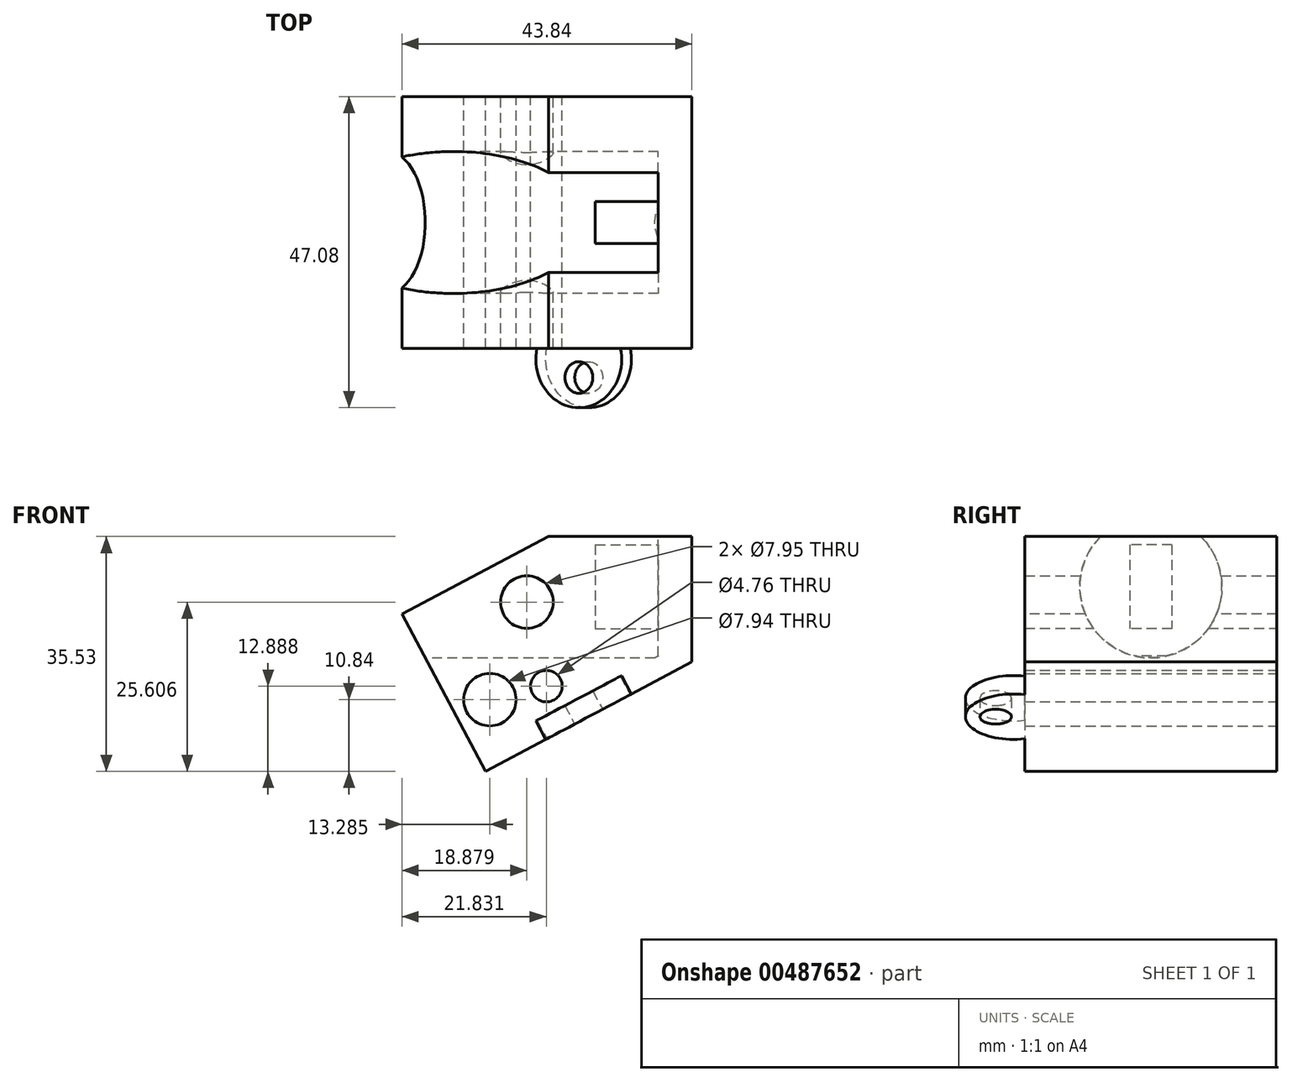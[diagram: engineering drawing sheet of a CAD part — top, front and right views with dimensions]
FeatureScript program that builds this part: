
annotation { "Feature Type Name" : "Feature", "Feature Type Description" : "" }
export const myFeature = defineFeature(function(context is Context, id is Id, definition is map)
    precondition{}
    {
        {
            var Q0;
            Q0=qCreatedBy(makeId("Top.planeOp"),FACE);
            var sketch = newSketch(context, id + "F0", { "sketchPlane" : qUnion([Q0])});
            skLineSegment(sketch, "E0.bottom", {"start": v(0, 0) * mm, "end": v(50.8, 0) * mm});
            skLineSegment(sketch, "E0.top", {"start": v(0, -38.1) * mm, "end": v(50.8, -38.1) * mm});
            skLineSegment(sketch, "E0.left", {"start": v(0, 0) * mm, "end": v(0, -38.1) * mm});
            skLineSegment(sketch, "E0.right", {"start": v(50.8, 0) * mm, "end": v(50.8, -38.1) * mm});
            skSolve(sketch);
        }
        {
            var Q0;
            Q0 = qSketchRegion(id + "F0", true);
            extrude(context, id + "F1", {"entities" : qUnion([Q0]), "depth" : 50.8 * mm, "offsetDistance" : 25.4 * mm});
        }
        {
            var Q0;
            Q0=makeQuery(id+"F1.opExtrude","SWEPT_FACE",FACE,{"disambiguationData":[OSD([sQuery(id+"F0.wireOp",EDGE,"E0.top")])]});
            var sketch = newSketch(context, id + "F2", { "sketchPlane" : qUnion([Q0])});
            skLineSegment(sketch, "E1", {"start": v(29.5, 53.9) * mm, "end": v(29.5, 32.46) * mm, "construction": true});
            skLineSegment(sketch, "E2", {"start": v(45.7, 53.9) * mm, "end": v(45.7, 32.46) * mm});
            skLineSegment(sketch, "E3", {"start": v(29.5, 32.46) * mm, "end": v(5.38, 32.46) * mm, "construction": true});
            skLineSegment(sketch, "E4", {"start": v(5.38, 32.46) * mm, "end": v(5.38, 41.35) * mm});
            skPoint(sketch, "E5.startSnap0", {"position": v(5.38, 36.9) * mm});
            skLineSegment(sketch, "E6", {"start": v(5.38, 41.35) * mm, "end": v(29.5, 53.9) * mm});
            skLineSegment(sketch, "E7", {"start": v(5.38, 32.46) * mm, "end": v(45.7, 32.46) * mm});
            skLineSegment(sketch, "E8", {"start": v(29.5, 53.9) * mm, "end": v(45.7, 53.9) * mm});
            skLineSegment(sketch, "E9", {"start": v(45.7, 43.18) * mm, "end": v(-3.01, 43.18) * mm, "construction": true});
            skSolve(sketch);
        }
        {
            var Q0;
            Q0=makeQuery(id+"F1.opExtrude","SWEPT_FACE",FACE,{"disambiguationData":[OSD([sQuery(id+"F0.wireOp",EDGE,"E0.left")])]});
            var sketch = newSketch(context, id + "F3", { "sketchPlane" : qUnion([Q0])});
            skLineSegment(sketch, "E10", {"start": v(38.1, 43.18) * mm, "end": v(0, 43.18) * mm, "construction": true});
            skLineSegment(sketch, "E11", {"start": v(19.05, 50.8) * mm, "end": v(19.05, 0) * mm, "construction": true});
            skCircle(sketch, "E12", {"center": v(19.05, 43.18) * mm, "radius": 10.74 * mm});
            skSolve(sketch);
        }
        {
            var Q0;
            Q0 = qSketchRegion(id + "F3", true);
            extrude(context, id + "F4", {"entities" : qUnion([Q0]), "operationType" : NewBodyOperationType.REMOVE, "oppositeDirection" : true, "depth" : 40.64 * mm, "offsetDistance" : 25.4 * mm});
        }
        {
            var Q0;
            Q0 = qSketchRegion(id + "F3", true);
            extrude(context, id + "F5", {"entities" : qUnion([Q0]), "operationType" : NewBodyOperationType.REMOVE, "oppositeDirection" : true, "depth" : 45.72 * mm, "offsetDistance" : 25.4 * mm});
        }
        {
            var Q0;
            Q0=makeQuery(id+"F2.imprint","IMPRINT",FACE,{"disambiguationData":[TD([[makeQuery(id+"F2.imprint","IMPRINT",EDGE,{"derivedFrom":sQuery(id+"F2.wireOp",EDGE,"E2")}),1.0]])]});
            var sketch = newSketch(context, id + "F6", { "sketchPlane" : qUnion([Q0])});
            skLineSegment(sketch, "E13", {"start": v(29.63, 51.07) * mm, "end": v(-5.3, 32.58) * mm});
            skLineSegment(sketch, "E14", {"start": v(-5.3, 32.58) * mm, "end": v(-5.3, 56.5) * mm});
            skLineSegment(sketch, "E15", {"start": v(-5.3, 56.5) * mm, "end": v(29.3, 56.5) * mm});
            skLineSegment(sketch, "E16", {"start": v(29.3, 56.5) * mm, "end": v(29.63, 51.07) * mm});
            skSolve(sketch);
        }
        {
            var Q0;
            Q0 = qSketchRegion(id + "F6", true);
            extrude(context, id + "F7", {"entities" : qUnion([Q0]), "operationType" : NewBodyOperationType.REMOVE, "endBound" : BoundingType.THROUGH_ALL, "oppositeDirection" : true, "depth" : 25.4 * mm, "offsetDistance" : 25.4 * mm});
        }
        {
            var Q0;
            Q0=makeQuery(id+"F1.opExtrude","SWEPT_FACE",FACE,{"disambiguationData":[OSD([sQuery(id+"F0.wireOp",EDGE,"E0.top")])]});
            var sketch = newSketch(context, id + "F8", { "sketchPlane" : qUnion([Q0])});
            skLineSegment(sketch, "E17", {"start": v(0, 35.38) * mm, "end": v(12.6, 11.58) * mm});
            skLineSegment(sketch, "E18", {"start": v(12.6, 11.58) * mm, "end": v(52.93, 32.94) * mm});
            skLineSegment(sketch, "E19", {"start": v(52.93, 32.94) * mm, "end": v(52.93, -3.73) * mm});
            skLineSegment(sketch, "E20", {"start": v(52.93, -3.73) * mm, "end": v(-3.8, -3.73) * mm});
            skLineSegment(sketch, "E21", {"start": v(-3.8, -3.73) * mm, "end": v(-3.8, 35.25) * mm});
            skLineSegment(sketch, "E22", {"start": v(-3.8, 35.25) * mm, "end": v(0, 35.38) * mm});
            skSolve(sketch);
        }
        {
            var Q0;
            Q0=makeQuery(id+"F5.boolean.opBoolean","COPY",FACE,{"derivedFrom":makeQuery(id+"F5.opExtrude","CAP_FACE",FACE,{"disambiguationData":[OSD([sQuery(id+"F3.wireOp",EDGE,"E12")])],"isStart":false})});
            var sketch = newSketch(context, id + "F9", { "sketchPlane" : qUnion([Q0])});
            skLineSegment(sketch, "E23.bottom", {"start": v(15.88, 49.53) * mm, "end": v(22.23, 49.53) * mm});
            skLineSegment(sketch, "E23.top", {"start": v(15.88, 36.83) * mm, "end": v(22.23, 36.83) * mm});
            skLineSegment(sketch, "E23.left", {"start": v(15.88, 49.53) * mm, "end": v(15.88, 36.83) * mm});
            skLineSegment(sketch, "E23.right", {"start": v(22.23, 49.53) * mm, "end": v(22.23, 36.83) * mm});
            skLineSegment(sketch, "E24", {"start": v(19.05, 43.18) * mm, "end": v(19.05, 52.46) * mm, "construction": true});
            skLineSegment(sketch, "E25", {"start": v(19.05, 43.18) * mm, "end": v(28.74, 43.18) * mm, "construction": true});
            skSolve(sketch);
        }
        {
            var Q0;
            Q0 = qSketchRegion(id + "F9", true);
            extrude(context, id + "F10", {"entities" : qUnion([Q0]), "operationType" : NewBodyOperationType.ADD, "depth" : 9.52 * mm, "offsetDistance" : 25.4 * mm});
        }
        {
            var Q0;
            Q0 = qSketchRegion(id + "F8", true);
            extrude(context, id + "F11", {"entities" : qUnion([Q0]), "operationType" : NewBodyOperationType.REMOVE, "endBound" : BoundingType.THROUGH_ALL, "oppositeDirection" : true, "depth" : 25.4 * mm, "offsetDistance" : 25.4 * mm});
        }
        {
            var Q0;
            {var subQ2=sQuery(id+"F2.wireOp",EDGE,"E4");Q0=makeQuery(id+"F2.imprint","IMPRINT",FACE,{"disambiguationData":[TD([[makeQuery(id+"F2.imprint","IMPRINT",EDGE,{"derivedFrom":subQ2}),1.0]])]});}
            var sketch = newSketch(context, id + "F12", { "sketchPlane" : qUnion([Q0])});
            skLineSegment(sketch, "E26", {"start": v(5.52, 41.79) * mm, "end": v(21.07, 12.42) * mm});
            skLineSegment(sketch, "E27", {"start": v(21.07, 12.42) * mm, "end": v(9.08, 6.07) * mm});
            skLineSegment(sketch, "E28", {"start": v(9.08, 6.07) * mm, "end": v(-6.5, 35.47) * mm});
            skLineSegment(sketch, "E29", {"start": v(-6.5, 35.47) * mm, "end": v(5.52, 41.79) * mm});
            skSolve(sketch);
        }
        {
            var Q0;
            Q0 = qSketchRegion(id + "F12", true);
            extrude(context, id + "F13", {"entities" : qUnion([Q0]), "operationType" : NewBodyOperationType.REMOVE, "endBound" : BoundingType.THROUGH_ALL, "oppositeDirection" : true, "depth" : 25.4 * mm, "offsetDistance" : 25.4 * mm});
        }
        {
            var Q0;
            Q0=makeQuery(id+"F1.opExtrude","SWEPT_BODY",BODY,{"disambiguationData":[OSD([sQuery(id+"F0.wireOp",EDGE,"E0.bottom"),sQuery(id+"F0.wireOp",EDGE,"E0.top"),sQuery(id+"F0.wireOp",EDGE,"E0.left"),sQuery(id+"F0.wireOp",EDGE,"E0.right")])]});
            var Q1;
            Q1=makeQuery(id+"F13.boolean.opBoolean","INTERSECT",EDGE,{"derivedFrom":[makeQuery(id+"F11.boolean.opBoolean","COPY",FACE,{"derivedFrom":makeQuery(id+"F11.opExtrude","SWEPT_FACE",FACE,{"disambiguationData":[OSD([sQuery(id+"F8.wireOp",EDGE,"E18")])]})}),makeQuery(id+"F13.opExtrude","SWEPT_FACE",FACE,{"disambiguationData":[OSD([sQuery(id+"F12.wireOp",EDGE,"E26")])]})]});
            transform(context, id + "F14", {"entities" : qUnion([Q0]), "transformType" : TransformType.TRANSLATION_3D, "dx" : 12.8 * mm, "dy" : 76.1 * mm, "dz" : -11.5 * mm, "makeCopy" : false});
        }
        {
            var Q0;
            Q0=makeQuery(id+"F11.boolean.opBoolean","INTERSECT",EDGE,{"derivedFrom":[makeQuery(id+"F1.opExtrude","SWEPT_FACE",FACE,{"disambiguationData":[OSD([sQuery(id+"F0.wireOp",EDGE,"E0.right")])]}),makeQuery(id+"F11.opExtrude","SWEPT_FACE",FACE,{"disambiguationData":[OSD([sQuery(id+"F8.wireOp",EDGE,"E18")])]})]});
            cPoint(context, id + "F15", {"entities" : qUnion([Q0]), "parameter" : 0.5});
        }
        {
            var Q0;
            Q0=makeQuery(id+"F1.opExtrude","SWEPT_BODY",BODY,{"disambiguationData":[OSD([sQuery(id+"F0.wireOp",EDGE,"E0.bottom"),sQuery(id+"F0.wireOp",EDGE,"E0.top"),sQuery(id+"F0.wireOp",EDGE,"E0.left"),sQuery(id+"F0.wireOp",EDGE,"E0.right")])]});
            var Q1;
            Q1 = qCreatedBy(id + "F15" ,VERTEX);
            transform(context, id + "F16", {"entities" : qUnion([Q0]), "transformType" : TransformType.TRANSLATION_3D, "dx" : -7.9 * mm, "dy" : 0 * mm, "dz" : 0 * mm, "makeCopy" : false});
        }
        {
            var Q0;
            Q0=makeQuery(id+"F1.opExtrude","SWEPT_BODY",BODY,{"disambiguationData":[OSD([sQuery(id+"F0.wireOp",EDGE,"E0.bottom"),sQuery(id+"F0.wireOp",EDGE,"E0.top"),sQuery(id+"F0.wireOp",EDGE,"E0.left"),sQuery(id+"F0.wireOp",EDGE,"E0.right")])]});
            transform(context, id + "F17", {"entities" : qUnion([Q0]), "transformType" : TransformType.TRANSLATION_3D, "dx" : 1.3 * mm, "dy" : 0 * mm, "dz" : -3.7 * mm, "makeCopy" : false});
        }
        {
            var Q0;
            Q0=makeQuery(id+"F1.opExtrude","SWEPT_BODY",BODY,{"disambiguationData":[OSD([sQuery(id+"F0.wireOp",EDGE,"E0.bottom"),sQuery(id+"F0.wireOp",EDGE,"E0.top"),sQuery(id+"F0.wireOp",EDGE,"E0.left"),sQuery(id+"F0.wireOp",EDGE,"E0.right")])]});
            transform(context, id + "F18", {"entities" : qUnion([Q0]), "transformType" : TransformType.TRANSLATION_3D, "dx" : 0.5 * mm, "dy" : 0 * mm, "dz" : -3.8 * mm, "makeCopy" : false});
        }
        {
            var Q0;
            Q0=makeQuery(id+"F1.opExtrude","SWEPT_BODY",BODY,{"disambiguationData":[OSD([sQuery(id+"F0.wireOp",EDGE,"E0.bottom"),sQuery(id+"F0.wireOp",EDGE,"E0.top"),sQuery(id+"F0.wireOp",EDGE,"E0.left"),sQuery(id+"F0.wireOp",EDGE,"E0.right")])]});
            var Q1;
            Q1=makeQuery(id+"FGyysRZlWEtIOdi_1.opExtrude","SWEPT_BODY",BODY,{"disambiguationData":[OSD([sQuery(id+"F0.wireOp",EDGE,"E0.bottom"),sQuery(id+"F8.wireOp",EDGE,"E18"),sQuery(id+"FFfA244eIHv1Rg5_1.wireOp",EDGE,"84cc6b51-f840-485a-b451-296fac33cd6d0.MirrorC"),sQuery(id+"FFfA244eIHv1Rg5_1.wireOp",EDGE,"84cc6b51-f840-485a-b451-296fac33cd6d1.MirrorCS")])]});
            var Q2;
            Q2=makeQuery(id+"FGyysRZlWEtIOdi_1.opExtrude","SWEPT_BODY",BODY,{"disambiguationData":[OSD([sQuery(id+"F8.wireOp",EDGE,"E18"),sQuery(id+"FFfA244eIHv1Rg5_1.wireOp",EDGE,"nyTDxEeG-qcKT-SzzJ-3wPE-0a3jBs2usvt1"),sQuery(id+"FFfA244eIHv1Rg5_1.wireOp",EDGE,"AyRyBbrL-wrfp-xTRg-XlCM-ypKMbF0xuXCW")])]});
            transform(context, id + "F19", {"entities" : qUnion([Q0, Q1, Q2]), "transformType" : TransformType.TRANSLATION_3D, "dx" : -1.02 * mm, "dy" : 0 * mm, "dz" : 4.06 * mm, "makeCopy" : false});
        }
        {
            var Q0;
            Q0=makeQuery(id+"F1.opExtrude","SWEPT_FACE",FACE,{"disambiguationData":[OSD([sQuery(id+"F0.wireOp",EDGE,"E0.bottom")])]});
            var sketch = newSketch(context, id + "F20", { "sketchPlane" : qUnion([Q0])});
            skCircle(sketch, "E30", {"center": v(-34.47, 13.22) * mm, "radius": 2.38 * mm});
            skCircle(sketch, "E31", {"center": v(-25.93, 11.17) * mm, "radius": 3.97 * mm});
            skCircle(sketch, "E32", {"center": v(-31.52, 25.94) * mm, "radius": 3.98 * mm});
            skSolve(sketch);
        }
        {
            var Q0;
            Q0 = qSketchRegion(id + "F20", true);
            extrude(context, id + "F21", {"entities" : qUnion([Q0]), "operationType" : NewBodyOperationType.REMOVE, "endBound" : BoundingType.THROUGH_ALL, "oppositeDirection" : true, "depth" : 25.4 * mm, "offsetDistance" : 25.4 * mm});
        }
        {
            var Q0;
            Q0=makeQuery(id+"F11.boolean.opBoolean","COPY",FACE,{"derivedFrom":makeQuery(id+"F11.opExtrude","SWEPT_FACE",FACE,{"disambiguationData":[OSD([sQuery(id+"F8.wireOp",EDGE,"E18")])]})});
            extrude(context, id + "F22", {"entities" : qUnion([Q0]), "operationType" : NewBodyOperationType.ADD, "oppositeDirection" : true, "depth" : 3.17 * mm, "offsetDistance" : 25.4 * mm});
        }
        {
            var Q0;
            Q0=makeQuery(id+"F11.boolean.opBoolean","COPY",FACE,{"derivedFrom":makeQuery(id+"F11.opExtrude","SWEPT_FACE",FACE,{"disambiguationData":[OSD([sQuery(id+"F8.wireOp",EDGE,"E18")])]})});
            var sketch = newSketch(context, id + "F23", { "sketchPlane" : qUnion([Q0])});
            skLineSegment(sketch, "E33", {"start": v(40.14, -38) * mm, "end": v(40.14, -76.1) * mm, "construction": true});
            skLineSegment(sketch, "E34", {"start": v(57.81, -57.05) * mm, "end": v(22.47, -57.05) * mm, "construction": true});
            skLineSegment(sketch, "E35", {"start": v(47.28, -38) * mm, "end": v(47.28, -76.1) * mm, "construction": true});
            skLineSegment(sketch, "E36", {"start": v(32.98, -38) * mm, "end": v(32.98, -76.1) * mm, "construction": true});
            skLineSegment(sketch, "E37", {"start": v(40.14, -38) * mm, "end": v(40.14, -29.19) * mm, "construction": true});
            skLineSegment(sketch, "E38", {"start": v(46.83, -33.6) * mm, "end": v(33.42, -33.6) * mm, "construction": true});
            skPoint(sketch, "E38.startSnap0", {"position": v(40.14, -33.6) * mm});
            skCircle(sketch, "E39", {"center": v(40.14, -33.6) * mm, "radius": 2.39 * mm});
            skArc(sketch, "E40", {"start": v(47.28, -38) * mm, "mid": v(40.13, -29.02) * mm, "end": v(32.98, -38) * mm});
            skArc(sketch, "E41.MirrorCS", {"start": v(47.28, -76.1) * mm, "mid": v(40.13, -85.08) * mm, "end": v(32.98, -76.1) * mm});
            skCircle(sketch, "E42.MirrorC", {"center": v(40.14, -80.5) * mm, "radius": 2.39 * mm});
            skSolve(sketch);
        }
        {
            var Q0;
            Q0=makeQuery(id+"F23.imprint","IMPRINT",FACE,{"disambiguationData":[TD([[makeQuery(id+"F23.imprint","IMPRINT",EDGE,{"derivedFrom":sQuery(id+"F23.wireOp",EDGE,"E39")}),-1.0]])]});
            var Q1;
            {var subQ0=sQuery(id+"F23.wireOp",EDGE,"E41.MirrorCS");Q1=makeQuery(id+"F23.imprint","IMPRINT",FACE,{"disambiguationData":[TD([[makeQuery(id+"F23.imprint","IMPRINT",EDGE,{"derivedFrom":subQ0}),-1.0]])]});}
            extrude(context, id + "F24", {"entities" : qUnion([Q0, Q1]), "operationType" : NewBodyOperationType.ADD, "oppositeDirection" : true, "depth" : 3.17 * mm, "offsetDistance" : 25.4 * mm});
        }
    });
